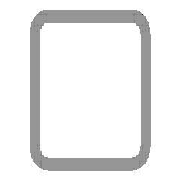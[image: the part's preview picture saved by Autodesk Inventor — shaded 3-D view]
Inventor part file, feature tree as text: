
AUTODESK INVENTOR PART (.ipt)
format: ipt  version: 2022 (Build 260153000, 153)  size: 179,200 bytes
history: native  units: mm (DEFAULTED — no unit token found)
features: other x5, sketch x2, sweep x1, plane x1
ambient origin geometry x8: Origin, YZ Plane, XZ Plane, XY Plane, X Axis, Y Axis, Z Axis, Center Point
bodies: Solid1 (feature_tree), Body (feature_tree)
feature tree (9):
  parser-record x1  (decoder bookkeeping rows leaked as tree rows — omitted from the tree; the rows remain in map.json)
  other  "Driven Length"
  other  "Start Plane"
  other  "End Plane"
  sweep  "Sweep Path"
  other  "Orientation Work Plane"
  sketch  "Sketch3"  dims[d7=7.5mm d10=40.0mm]
  plane  "Work Plane3"
  sketch  "Sketch4"  dims[d11=40.0mm d12=5.0mm d13=-0.0mm d14=3875.406592mm d15=20.0mm d16=20.0mm d17=90.0deg d18=3875.406592mm d19=0.0mm d20=0.0mm]
